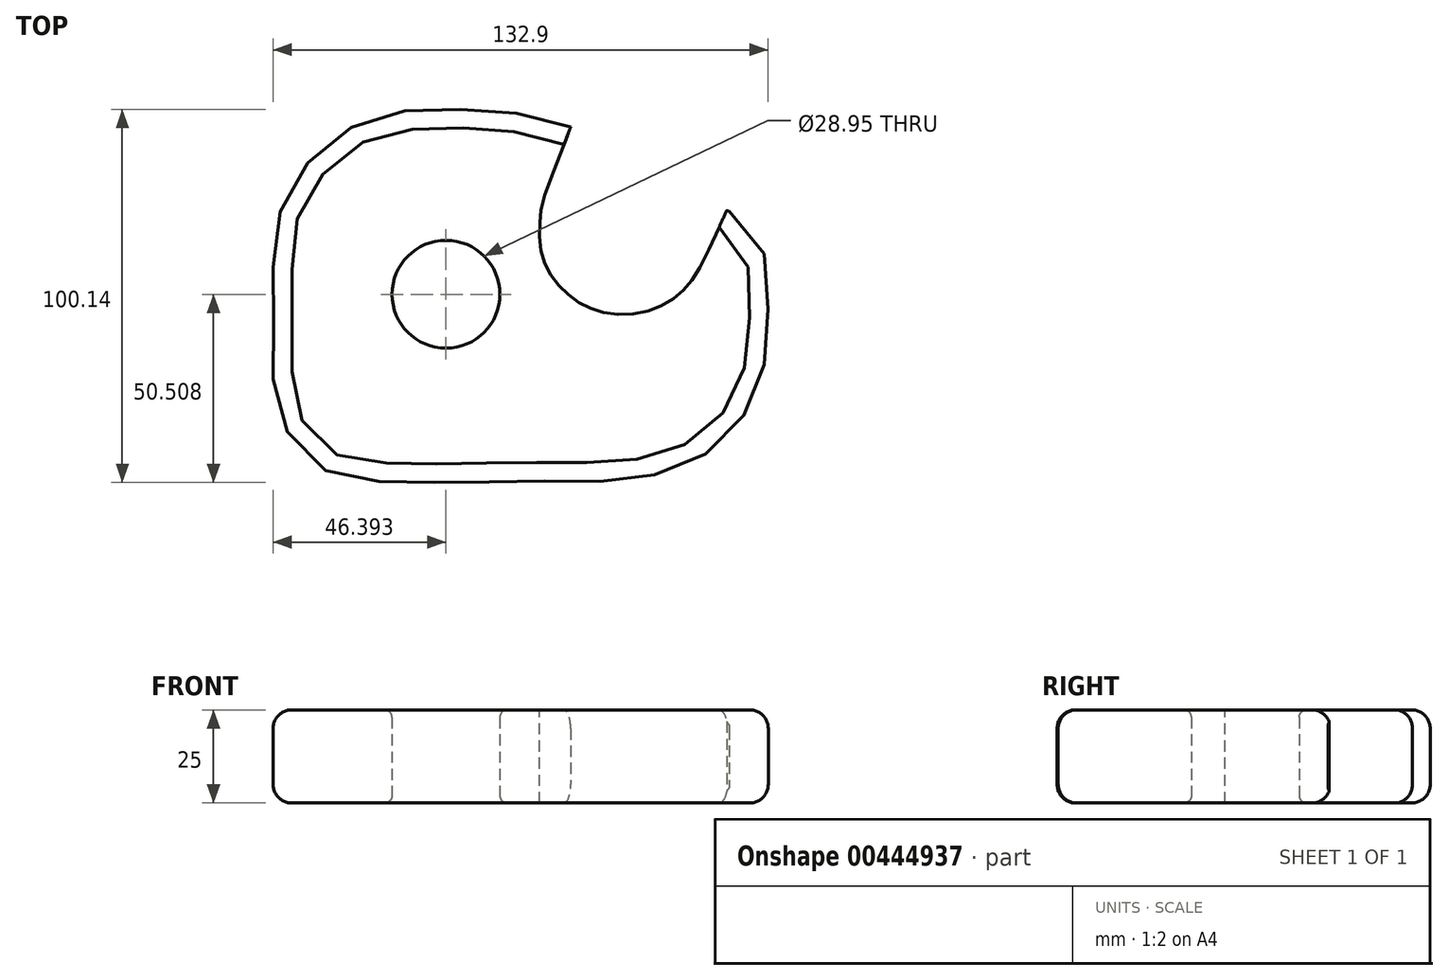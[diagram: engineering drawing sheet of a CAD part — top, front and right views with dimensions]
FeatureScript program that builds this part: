
annotation { "Feature Type Name" : "Feature", "Feature Type Description" : "" }
export const myFeature = defineFeature(function(context is Context, id is Id, definition is map)
    precondition{}
    {
        {
            var Q0;
            Q0=qCreatedBy(makeId("Top.planeOp"),FACE);
            var sketch = newSketch(context, id + "F0", { "sketchPlane" : qUnion([Q0])});
            skFitSpline(sketch, "E0", {"points": [v(4.77, 37.02) * mm, v(-2.58, 17.35) * mm, v(-3.4, 12.37) * mm, v(-3.6, 7.05) * mm, v(-2.66, 1.7) * mm, v(-0.5, -2.6) * mm, v(2.5, -6.41) * mm, v(6.26, -9.56) * mm, v(10.63, -11.86) * mm, v(15.87, -13.16) * mm, v(22.48, -12.98) * mm, v(28.2, -11.41) * mm, v(33, -8.54) * mm, v(36.44, -5.15) * mm, v(39.83, 0) * mm, v(46.65, 14.6) * mm], "startDerivative": vector(-73.5, -200.14) * mm, "endDerivative": vector(73.19, 160.43) * mm});
            skFitSpline(sketch, "E1", {"points": [v(46.65, 14.6) * mm, v(47.4, 14.4) * mm], "startDerivative": vector(0.18, 0.37) * mm, "endDerivative": vector(0.18, 0.37) * mm});
            skFitSpline(sketch, "E2", {"points": [v(47.4, 14.4) * mm, v(53, 8.67) * mm, v(55.85, 4.37) * mm, v(57.23, 1.23) * mm, v(57.45, -20.52) * mm, v(55.51, -31.16) * mm, v(50.02, -42.24) * mm, v(37.81, -52.53) * mm, v(18.69, -57.77) * mm, v(0.88, -57.92) * mm, v(-48.95, -57.9) * mm, v(-60.35, -55.42) * mm, v(-65.3, -52.27) * mm, v(-73.96, -39.76) * mm, v(-74.97, -28.45) * mm, v(-74.92, 4.76) * mm, v(-73.32, 13.85) * mm, v(-67.38, 25.41) * mm, v(-55.99, 35.8) * mm, v(-48.2, 39.62) * mm, v(-40.3, 41.25) * mm, v(-29.82, 41.75) * mm, v(-19.81, 41.67) * mm, v(-9.58, 40.66) * mm, v(4.77, 37.02) * mm], "startDerivative": vector(198.6, -182.1) * mm, "endDerivative": vector(339.02, -84.44) * mm});
            skCircle(sketch, "E3", {"center": v(-28.69, -7.85) * mm, "radius": 14.48 * mm});
            skSolve(sketch);
        }
        {
            var Q0;
            Q0 = qSketchRegion(id + "F0", true);
            extrude(context, id + "F1", {"entities" : qUnion([Q0]), "depth" : 25 * mm});
        }
        {
            var Q0;
            Q0=makeQuery(id+"F1.opExtrude","CAP_EDGE",EDGE,{"disambiguationData":[OSD([sQuery(id+"F0.wireOp",EDGE,"E2")])],"isStart":false});
            var Q1;
            Q1=makeQuery(id+"F1.opExtrude","CAP_EDGE",EDGE,{"disambiguationData":[OSD([sQuery(id+"F0.wireOp",EDGE,"E2")])],"isStart":true});
            fillet(context, id + "F2", {"entities" : qUnion([Q0, Q1]), "radius" : 5 * mm, "tangentPropagation" : true, "allowEdgeOverflow" : false});
        }
        {
            var Q0;
            Q0=makeQuery(id+"F1.opExtrude","SWEPT_FACE",FACE,{"disambiguationData":[OSD([sQuery(id+"F0.wireOp",EDGE,"E3")])]});
            fillet(context, id + "F3", {"entities" : qUnion([Q0]), "radius" : 2 * mm, "tangentPropagation" : true, "allowEdgeOverflow" : false});
        }
    });
